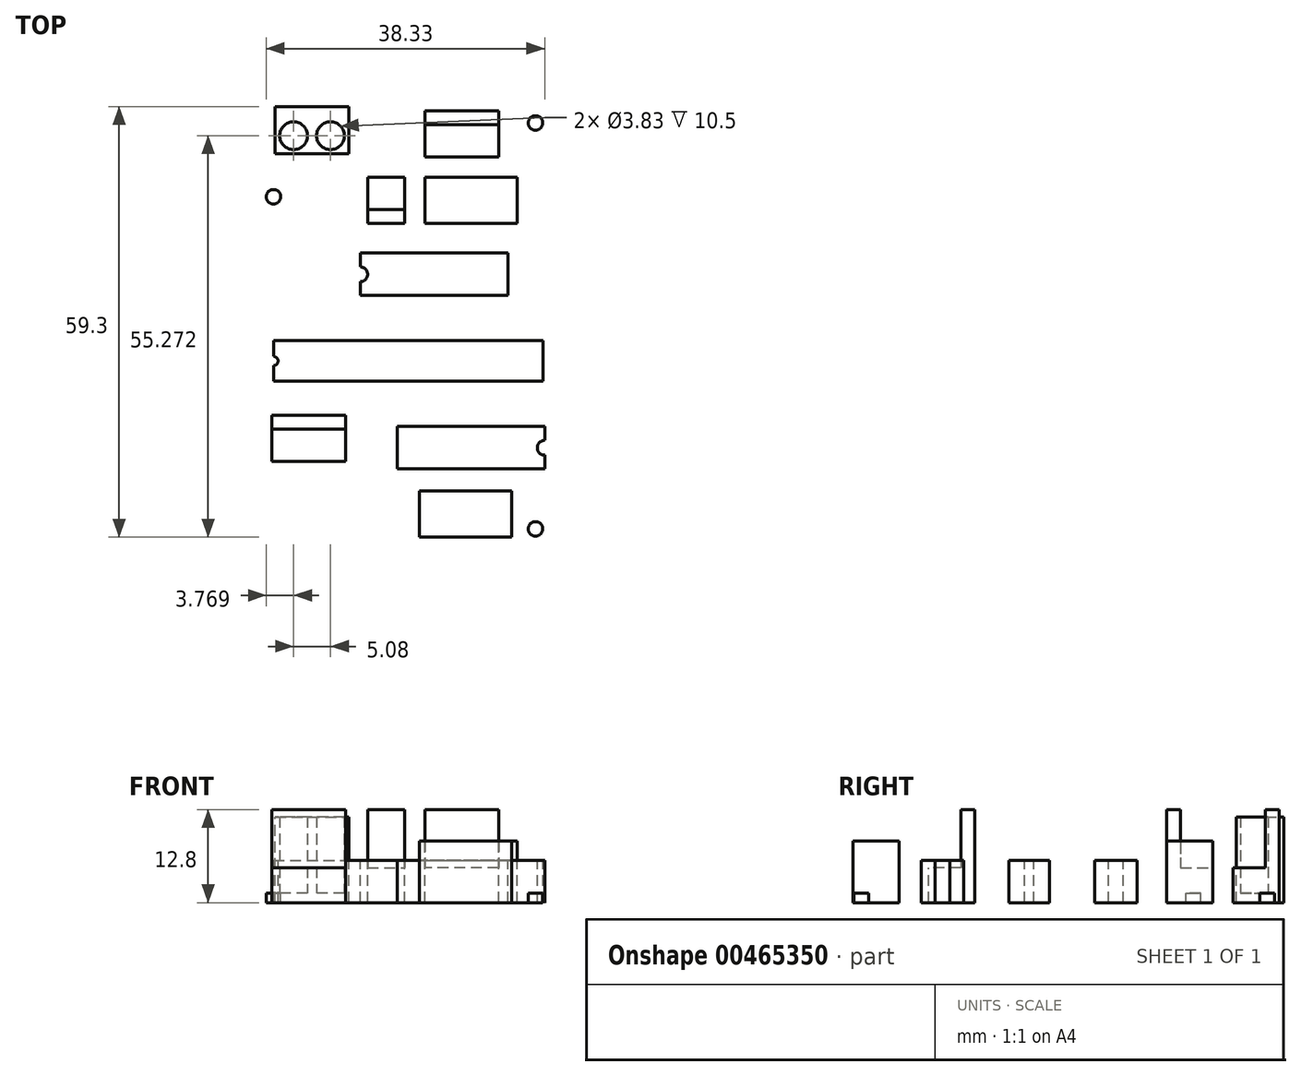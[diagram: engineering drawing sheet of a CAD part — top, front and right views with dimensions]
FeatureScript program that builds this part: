
annotation { "Feature Type Name" : "Feature", "Feature Type Description" : "" }
export const myFeature = defineFeature(function(context is Context, id is Id, definition is map)
    precondition{}
    {
        {
            var Q0;
            Q0=qCreatedBy(makeId("Top.planeOp"),FACE);
            var sketch = newSketch(context, id + "F0", { "sketchPlane" : qUnion([Q0])});
            skLineSegment(sketch, "E0", {"start": v(-20.57, 30.6) * mm, "end": v(20.57, 30.6) * mm});
            skLineSegment(sketch, "E1", {"start": v(20.57, 30.6) * mm, "end": v(20.57, -30.6) * mm});
            skLineSegment(sketch, "E2", {"start": v(20.57, -30.6) * mm, "end": v(-20.57, -30.6) * mm});
            skLineSegment(sketch, "E3", {"start": v(-20.57, -30.6) * mm, "end": v(-20.57, 30.6) * mm});
            skSolve(sketch);
        }
        {
            var Q0;
            Q0 = qSketchRegion(id + "F0", true);
            extrude(context, id + "F1", {"entities" : qUnion([Q0]), "depth" : 1.3 * mm});
        }
        {
            var Q0;
            Q0=makeQuery(id+"F1.opExtrude","CAP_FACE",FACE,{"disambiguationData":[OSD([sQuery(id+"F0.wireOp",EDGE,"E0"),sQuery(id+"F0.wireOp",EDGE,"E1"),sQuery(id+"F0.wireOp",EDGE,"E2"),sQuery(id+"F0.wireOp",EDGE,"E3")])],"isStart":false});
            var sketch = newSketch(context, id + "F2", { "sketchPlane" : qUnion([Q0])});
            skLineSegment(sketch, "E4", {"start": v(-20.57, 30.6) * mm, "end": v(20.57, 30.6) * mm});
            skLineSegment(sketch, "E5", {"start": v(20.57, 30.6) * mm, "end": v(20.57, -30.6) * mm});
            skLineSegment(sketch, "E6", {"start": v(20.57, -30.6) * mm, "end": v(-20.57, -30.6) * mm});
            skLineSegment(sketch, "E7", {"start": v(-20.57, -30.6) * mm, "end": v(-20.57, 30.6) * mm});
            skCircle(sketch, "E8", {"center": v(18.03, -28.58) * mm, "radius": 1 * mm});
            skCircle(sketch, "E9", {"center": v(18.03, 27.3) * mm, "radius": 1 * mm});
            skCircle(sketch, "E10", {"center": v(-18.03, 17.14) * mm, "radius": 1 * mm});
            skLineSegment(sketch, "E11", {"start": v(-17.8, 28.05) * mm, "end": v(-7.64, 28.05) * mm});
            skLineSegment(sketch, "E12", {"start": v(-17.8, 23.57) * mm, "end": v(-17.8, 23.08) * mm});
            skLineSegment(sketch, "E13", {"start": v(-17.8, 28.05) * mm, "end": v(-17.8, 27.57) * mm});
            skLineSegment(sketch, "E14", {"start": v(-17.8, 23.57) * mm, "end": v(-17.8, 27.57) * mm});
            skLineSegment(sketch, "E15", {"start": v(-7.64, 23.08) * mm, "end": v(-17.8, 23.08) * mm});
            skLineSegment(sketch, "E16", {"start": v(-7.64, 23.57) * mm, "end": v(-7.64, 23.08) * mm});
            skLineSegment(sketch, "E17", {"start": v(-7.64, 23.57) * mm, "end": v(-7.64, 27.57) * mm});
            skLineSegment(sketch, "E18", {"start": v(-7.64, 28.05) * mm, "end": v(-7.64, 27.57) * mm});
            skLineSegment(sketch, "E19", {"start": v(-7.64, 28.05) * mm, "end": v(-7.64, 29.58) * mm});
            skLineSegment(sketch, "E20", {"start": v(-17.8, 29.58) * mm, "end": v(-7.64, 29.58) * mm});
            skLineSegment(sketch, "E21", {"start": v(-17.8, 28.05) * mm, "end": v(-17.8, 29.58) * mm});
            skArc(sketch, "E22", {"start": v(-15.26, 23.64) * mm, "mid": v(-13.35, 25.55) * mm, "end": v(-15.26, 27.47) * mm});
            skArc(sketch, "E23", {"start": v(-15.26, 27.47) * mm, "mid": v(-17.18, 25.55) * mm, "end": v(-15.26, 23.64) * mm});
            skArc(sketch, "E24", {"start": v(-10.18, 23.64) * mm, "mid": v(-8.27, 25.55) * mm, "end": v(-10.18, 27.47) * mm});
            skArc(sketch, "E25", {"start": v(-10.18, 27.47) * mm, "mid": v(-12.1, 25.55) * mm, "end": v(-10.18, 23.64) * mm});
            skLineSegment(sketch, "E26", {"start": v(0, 13.46) * mm, "end": v(-5.08, 13.46) * mm});
            skLineSegment(sketch, "E27", {"start": v(-5.08, 13.46) * mm, "end": v(-5.08, 15.37) * mm});
            skLineSegment(sketch, "E28", {"start": v(-5.08, 15.37) * mm, "end": v(-5.08, 19.81) * mm});
            skLineSegment(sketch, "E29", {"start": v(-5.08, 19.81) * mm, "end": v(0, 19.81) * mm});
            skLineSegment(sketch, "E30", {"start": v(0, 19.81) * mm, "end": v(0, 15.37) * mm});
            skLineSegment(sketch, "E31", {"start": v(0, 15.37) * mm, "end": v(0, 13.46) * mm});
            skLineSegment(sketch, "E32", {"start": v(0, 15.37) * mm, "end": v(-5.08, 15.37) * mm});
            skLineSegment(sketch, "E33", {"start": v(-18.03, -6.1) * mm, "end": v(-18.03, -8.26) * mm});
            skArc(sketch, "E34", {"start": v(-18.03, -6.1) * mm, "mid": v(-17.4, -5.46) * mm, "end": v(-18.03, -4.83) * mm});
            skLineSegment(sketch, "E35", {"start": v(-18.03, -8.26) * mm, "end": v(19.05, -8.26) * mm});
            skLineSegment(sketch, "E36", {"start": v(-18.03, -2.67) * mm, "end": v(-18.03, -4.83) * mm});
            skLineSegment(sketch, "E37", {"start": v(-18.03, -2.67) * mm, "end": v(19.05, -2.67) * mm});
            skLineSegment(sketch, "E38", {"start": v(19.05, -2.67) * mm, "end": v(19.05, -8.26) * mm});
            skLineSegment(sketch, "E39", {"start": v(14.73, -29.72) * mm, "end": v(2.03, -29.72) * mm});
            skLineSegment(sketch, "E40", {"start": v(2.03, -29.72) * mm, "end": v(2.03, -27.81) * mm});
            skLineSegment(sketch, "E41", {"start": v(2.03, -27.81) * mm, "end": v(2.03, -23.37) * mm});
            skLineSegment(sketch, "E42", {"start": v(2.03, -23.37) * mm, "end": v(14.73, -23.37) * mm});
            skLineSegment(sketch, "E43", {"start": v(14.73, -23.37) * mm, "end": v(14.73, -27.81) * mm});
            skLineSegment(sketch, "E44", {"start": v(14.73, -27.81) * mm, "end": v(14.73, -29.72) * mm});
            skLineSegment(sketch, "E45", {"start": v(14.73, -27.81) * mm, "end": v(2.03, -27.81) * mm});
            skLineSegment(sketch, "E46", {"start": v(2.8, 19.81) * mm, "end": v(15.5, 19.81) * mm});
            skLineSegment(sketch, "E47", {"start": v(15.5, 19.81) * mm, "end": v(15.5, 17.9) * mm});
            skLineSegment(sketch, "E48", {"start": v(15.5, 17.9) * mm, "end": v(15.5, 13.46) * mm});
            skLineSegment(sketch, "E49", {"start": v(15.5, 13.46) * mm, "end": v(2.8, 13.46) * mm});
            skLineSegment(sketch, "E50", {"start": v(2.8, 13.46) * mm, "end": v(2.8, 17.9) * mm});
            skLineSegment(sketch, "E51", {"start": v(2.8, 17.9) * mm, "end": v(2.8, 19.81) * mm});
            skLineSegment(sketch, "E52", {"start": v(2.8, 17.9) * mm, "end": v(15.5, 17.9) * mm});
            skLineSegment(sketch, "E53", {"start": v(-18.29, -12.95) * mm, "end": v(-8.13, -12.95) * mm});
            skLineSegment(sketch, "E54", {"start": v(-8.13, -12.95) * mm, "end": v(-8.13, -14.86) * mm});
            skLineSegment(sketch, "E55", {"start": v(-8.13, -14.86) * mm, "end": v(-8.13, -19.3) * mm});
            skLineSegment(sketch, "E56", {"start": v(-8.13, -19.3) * mm, "end": v(-18.29, -19.3) * mm});
            skLineSegment(sketch, "E57", {"start": v(-18.29, -19.3) * mm, "end": v(-18.29, -14.86) * mm});
            skLineSegment(sketch, "E58", {"start": v(-18.29, -14.86) * mm, "end": v(-18.29, -12.95) * mm});
            skLineSegment(sketch, "E59", {"start": v(-18.29, -14.86) * mm, "end": v(-8.13, -14.86) * mm});
            skLineSegment(sketch, "E60", {"start": v(2.8, 28.96) * mm, "end": v(12.95, 28.96) * mm});
            skLineSegment(sketch, "E61", {"start": v(12.95, 28.96) * mm, "end": v(12.95, 27.05) * mm});
            skLineSegment(sketch, "E62", {"start": v(12.95, 27.05) * mm, "end": v(12.95, 22.6) * mm});
            skLineSegment(sketch, "E63", {"start": v(12.95, 22.6) * mm, "end": v(2.8, 22.6) * mm});
            skLineSegment(sketch, "E64", {"start": v(2.8, 22.6) * mm, "end": v(2.8, 27.05) * mm});
            skLineSegment(sketch, "E65", {"start": v(2.8, 27.05) * mm, "end": v(2.8, 28.96) * mm});
            skLineSegment(sketch, "E66", {"start": v(2.8, 27.05) * mm, "end": v(12.95, 27.05) * mm});
            skLineSegment(sketch, "E67", {"start": v(-1.02, -20.32) * mm, "end": v(19.3, -20.32) * mm});
            skLineSegment(sketch, "E68", {"start": v(19.3, -14.48) * mm, "end": v(-1.02, -14.48) * mm});
            skLineSegment(sketch, "E69", {"start": v(-1.02, -20.32) * mm, "end": v(-1.02, -14.48) * mm});
            skLineSegment(sketch, "E70", {"start": v(19.3, -20.32) * mm, "end": v(19.3, -18.41) * mm});
            skLineSegment(sketch, "E71", {"start": v(19.3, -14.48) * mm, "end": v(19.3, -16.38) * mm});
            skArc(sketch, "E72", {"start": v(19.3, -16.38) * mm, "mid": v(18.29, -17.4) * mm, "end": v(19.3, -18.41) * mm});
            skLineSegment(sketch, "E73", {"start": v(14.22, 9.4) * mm, "end": v(-6.1, 9.4) * mm});
            skLineSegment(sketch, "E74", {"start": v(-6.1, 3.56) * mm, "end": v(14.22, 3.56) * mm});
            skLineSegment(sketch, "E75", {"start": v(14.22, 9.4) * mm, "end": v(14.22, 3.56) * mm});
            skLineSegment(sketch, "E76", {"start": v(-6.1, 9.4) * mm, "end": v(-6.1, 7.5) * mm});
            skLineSegment(sketch, "E77", {"start": v(-6.1, 3.56) * mm, "end": v(-6.1, 5.46) * mm});
            skArc(sketch, "E78", {"start": v(-6.1, 5.46) * mm, "mid": v(-5.08, 6.48) * mm, "end": v(-6.1, 7.5) * mm});
            skSolve(sketch);
        }
        {
            var Q0;
            Q0=makeQuery(id+"F2.imprint","IMPRINT",FACE,{"disambiguationData":[TD([[makeQuery(id+"F2.imprint","IMPRINT",EDGE,{"derivedFrom":sQuery(id+"F2.wireOp",EDGE,"E10")}),-1.0]])]});
            var Q1;
            Q1=makeQuery(id+"F2.imprint","IMPRINT",FACE,{"disambiguationData":[TD([[makeQuery(id+"F2.imprint","IMPRINT",EDGE,{"derivedFrom":sQuery(id+"F2.wireOp",EDGE,"E9")}),-1.0]])]});
            var Q2;
            Q2=makeQuery(id+"F2.imprint","IMPRINT",FACE,{"disambiguationData":[TD([[makeQuery(id+"F2.imprint","IMPRINT",EDGE,{"derivedFrom":sQuery(id+"F2.wireOp",EDGE,"E8")}),-1.0]])]});
            extrude(context, id + "F3", {"entities" : qUnion([Q0, Q1, Q2]), "operationType" : NewBodyOperationType.REMOVE, "endBound" : BoundingType.UP_TO_NEXT, "oppositeDirection" : true, "depth" : 25 * mm});
        }
        {
            var Q0;
            Q0=makeQuery(id+"F2.imprint","IMPRINT",FACE,{"disambiguationData":[TD([[makeQuery(id+"F2.imprint","IMPRINT",EDGE,{"derivedFrom":sQuery(id+"F2.wireOp",EDGE,"E33")}),1.0]])]});
            var Q1;
            Q1=makeQuery(id+"F2.imprint","IMPRINT",FACE,{"disambiguationData":[TD([[makeQuery(id+"F2.imprint","IMPRINT",EDGE,{"derivedFrom":sQuery(id+"F2.wireOp",EDGE,"E73")}),1.0]])]});
            var Q2;
            Q2=makeQuery(id+"F2.imprint","IMPRINT",FACE,{"disambiguationData":[TD([[makeQuery(id+"F2.imprint","IMPRINT",EDGE,{"derivedFrom":sQuery(id+"F2.wireOp",EDGE,"E67")}),1.0]])]});
            extrude(context, id + "F4", {"entities" : qUnion([Q0, Q1, Q2]), "operationType" : NewBodyOperationType.ADD, "depth" : 4.5 * mm});
        }
        {
            var Q0;
            Q0=makeQuery(id+"F2.imprint","IMPRINT",FACE,{"disambiguationData":[TD([[makeQuery(id+"F2.imprint","IMPRINT",EDGE,{"derivedFrom":sQuery(id+"F2.wireOp",EDGE,"E11")}),1.0]])]});
            var Q1;
            Q1=makeQuery(id+"F2.imprint","IMPRINT",FACE,{"disambiguationData":[TD([[makeQuery(id+"F2.imprint","IMPRINT",EDGE,{"derivedFrom":sQuery(id+"F2.wireOp",EDGE,"E11")}),-1.0]])]});
            extrude(context, id + "F5", {"entities" : qUnion([Q0, Q1]), "operationType" : NewBodyOperationType.ADD, "depth" : 10.5 * mm});
        }
        {
            var Q0;
            Q0=makeQuery(id+"F2.imprint","IMPRINT",FACE,{"disambiguationData":[TD([[makeQuery(id+"F2.imprint","IMPRINT",EDGE,{"derivedFrom":sQuery(id+"F2.wireOp",EDGE,"E62")}),-1.0]])]});
            var Q1;
            Q1=makeQuery(id+"F2.imprint","IMPRINT",FACE,{"disambiguationData":[TD([[makeQuery(id+"F2.imprint","IMPRINT",EDGE,{"derivedFrom":sQuery(id+"F2.wireOp",EDGE,"E28")}),-1.0]])]});
            var Q2;
            Q2=makeQuery(id+"F2.imprint","IMPRINT",FACE,{"disambiguationData":[TD([[makeQuery(id+"F2.imprint","IMPRINT",EDGE,{"derivedFrom":sQuery(id+"F2.wireOp",EDGE,"E55")}),-1.0]])]});
            extrude(context, id + "F6", {"entities" : qUnion([Q0, Q1, Q2]), "operationType" : NewBodyOperationType.ADD, "depth" : 3.5 * mm});
        }
        {
            var Q0;
            Q0=makeQuery(id+"F2.imprint","IMPRINT",FACE,{"disambiguationData":[TD([[makeQuery(id+"F2.imprint","IMPRINT",EDGE,{"derivedFrom":sQuery(id+"F2.wireOp",EDGE,"E60")}),-1.0]])]});
            var Q1;
            Q1=makeQuery(id+"F2.imprint","IMPRINT",FACE,{"disambiguationData":[TD([[makeQuery(id+"F2.imprint","IMPRINT",EDGE,{"derivedFrom":sQuery(id+"F2.wireOp",EDGE,"E26")}),-1.0]])]});
            var Q2;
            Q2=makeQuery(id+"F2.imprint","IMPRINT",FACE,{"disambiguationData":[TD([[makeQuery(id+"F2.imprint","IMPRINT",EDGE,{"derivedFrom":sQuery(id+"F2.wireOp",EDGE,"E53")}),-1.0]])]});
            extrude(context, id + "F7", {"entities" : qUnion([Q0, Q1, Q2]), "operationType" : NewBodyOperationType.ADD, "depth" : 11.5 * mm});
        }
        {
            var Q0;
            Q0=makeQuery(id+"F2.imprint","IMPRINT",FACE,{"disambiguationData":[TD([[makeQuery(id+"F2.imprint","IMPRINT",EDGE,{"derivedFrom":sQuery(id+"F2.wireOp",EDGE,"E48")}),-1.0]])]});
            var Q1;
            Q1=makeQuery(id+"F2.imprint","IMPRINT",FACE,{"disambiguationData":[TD([[makeQuery(id+"F2.imprint","IMPRINT",EDGE,{"derivedFrom":sQuery(id+"F2.wireOp",EDGE,"E46")}),-1.0]])]});
            var Q2;
            Q2=makeQuery(id+"F2.imprint","IMPRINT",FACE,{"disambiguationData":[TD([[makeQuery(id+"F2.imprint","IMPRINT",EDGE,{"derivedFrom":sQuery(id+"F2.wireOp",EDGE,"E41")}),-1.0]])]});
            var Q3;
            Q3=makeQuery(id+"F2.imprint","IMPRINT",FACE,{"disambiguationData":[TD([[makeQuery(id+"F2.imprint","IMPRINT",EDGE,{"derivedFrom":sQuery(id+"F2.wireOp",EDGE,"E39")}),-1.0]])]});
            extrude(context, id + "F8", {"entities" : qUnion([Q0, Q1, Q2, Q3]), "operationType" : NewBodyOperationType.ADD, "depth" : 7.2 * mm});
        }
    });
